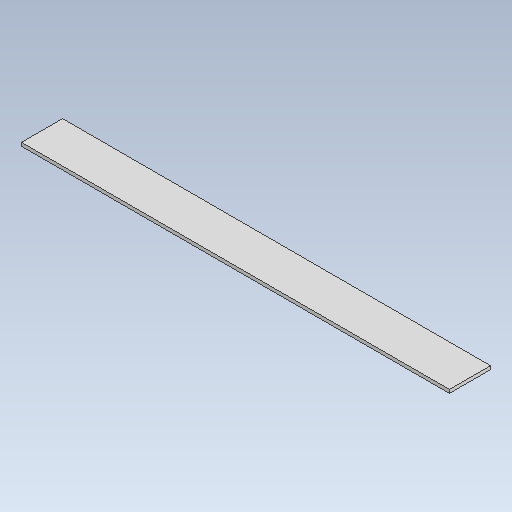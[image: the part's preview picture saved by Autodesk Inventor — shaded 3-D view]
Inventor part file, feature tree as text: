
AUTODESK INVENTOR PART (.ipt)
format: ipt  version: 2020.1 (Build 241239000, 239)  size: 96,768 bytes
history: native  units: mm
features: other x1, extrude x1, sketch x1
ambient origin geometry x8: Origin, YZ Plane, XZ Plane, XY Plane, X Axis, Y Axis, Z Axis, Center Point
bodies: Body1 (feature_tree)
feature tree (3):
  other  "Твердое тело1"
  extrude  "Выдавливание1"  Depth=96.0mm
  sketch  "Эскиз1"
